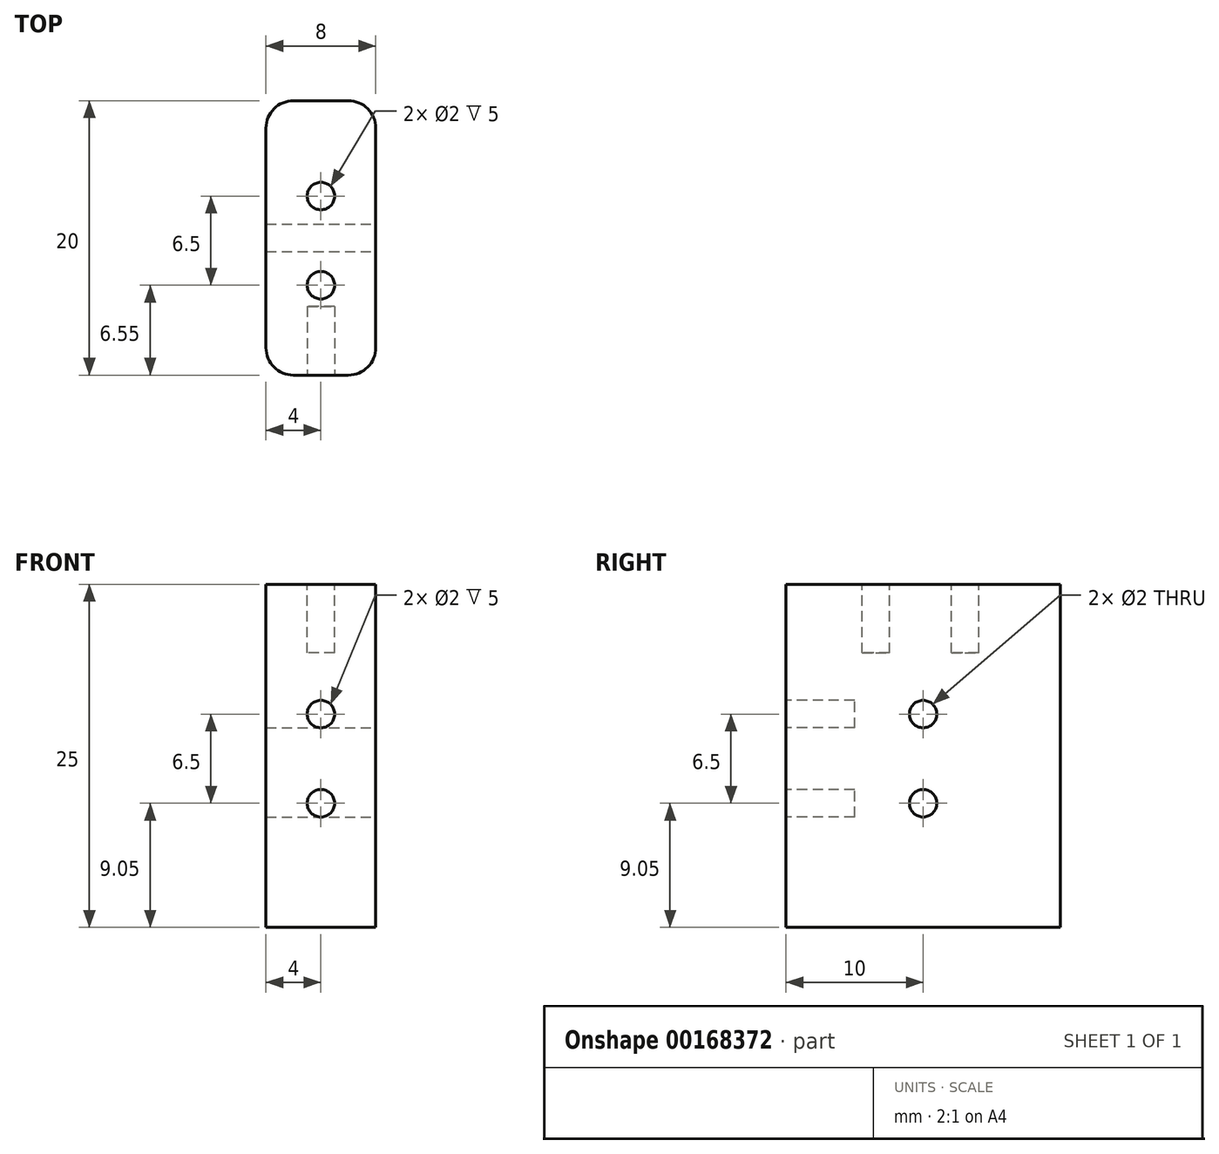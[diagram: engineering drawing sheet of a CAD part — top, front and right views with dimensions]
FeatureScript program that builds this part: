
annotation { "Feature Type Name" : "Feature", "Feature Type Description" : "" }
export const myFeature = defineFeature(function(context is Context, id is Id, definition is map)
    precondition{}
    {
        {
            var Q0;
            Q0=qCreatedBy(makeId("Right.planeOp"),FACE);
            var sketch = newSketch(context, id + "F0", { "sketchPlane" : qUnion([Q0])});
            skLineSegment(sketch, "E0.bottom", {"start": v(10, -12.5) * mm, "end": v(-10, -12.5) * mm});
            skLineSegment(sketch, "E0.top", {"start": v(10, 12.5) * mm, "end": v(-10, 12.5) * mm});
            skLineSegment(sketch, "E0.left", {"start": v(10, -12.5) * mm, "end": v(10, 12.5) * mm});
            skLineSegment(sketch, "E0.right", {"start": v(-10, -12.5) * mm, "end": v(-10, 12.5) * mm});
            skPoint(sketch, "E0.middle", {"position": v(0, 0) * mm});
            skSolve(sketch);
        }
        {
            var Q0;
            Q0 = qSketchRegion(id + "F0", true);
            extrude(context, id + "F1", {"entities" : qUnion([Q0]), "depth" : 8 * mm, "symmetric" : true});
        }
        {
            var Q0;
            Q0=makeQuery(id+"F1.opExtrude","CAP_FACE",FACE,{"disambiguationData":[OSD([sQuery(id+"F0.wireOp",EDGE,"E0.bottom"),sQuery(id+"F0.wireOp",EDGE,"E0.top"),sQuery(id+"F0.wireOp",EDGE,"E0.left"),sQuery(id+"F0.wireOp",EDGE,"E0.right")])],"isStart":false});
            var sketch = newSketch(context, id + "F2", { "sketchPlane" : qUnion([Q0])});
            skCircle(sketch, "E1", {"center": v(0, 3.05) * mm, "radius": 1 * mm});
            skCircle(sketch, "E2", {"center": v(0, -3.45) * mm, "radius": 1 * mm});
            skSolve(sketch);
        }
        {
            var Q0;
            Q0=makeQuery(id+"F1.opExtrude","SWEPT_FACE",FACE,{"disambiguationData":[OSD([sQuery(id+"F0.wireOp",EDGE,"E0.top")])]});
            var sketch = newSketch(context, id + "F3", { "sketchPlane" : qUnion([Q0])});
            skCircle(sketch, "E3", {"center": v(0, 3.05) * mm, "radius": 1 * mm});
            skCircle(sketch, "E4", {"center": v(0, -3.45) * mm, "radius": 1 * mm});
            skSolve(sketch);
        }
        {
            var Q0;
            Q0=makeQuery(id+"F1.opExtrude","SWEPT_FACE",FACE,{"disambiguationData":[OSD([sQuery(id+"F0.wireOp",EDGE,"E0.right")])]});
            var sketch = newSketch(context, id + "F4", { "sketchPlane" : qUnion([Q0])});
            skCircle(sketch, "E5", {"center": v(0, 3.05) * mm, "radius": 1 * mm});
            skCircle(sketch, "E6", {"center": v(0, -3.45) * mm, "radius": 1 * mm});
            skSolve(sketch);
        }
        {
            var Q0;
            Q0=makeQuery(id+"F2.imprint","IMPRINT",FACE,{"disambiguationData":[TD([[makeQuery(id+"F2.imprint","IMPRINT",EDGE,{"derivedFrom":sQuery(id+"F2.wireOp",EDGE,"E1")}),1.0]])]});
            var Q1;
            Q1=makeQuery(id+"F2.imprint","IMPRINT",FACE,{"disambiguationData":[TD([[makeQuery(id+"F2.imprint","IMPRINT",EDGE,{"derivedFrom":sQuery(id+"F2.wireOp",EDGE,"E2")}),1.0]])]});
            extrude(context, id + "F5", {"entities" : qUnion([Q0, Q1]), "operationType" : NewBodyOperationType.REMOVE, "oppositeDirection" : true, "depth" : 25 * mm});
        }
        {
            var Q0;
            Q0=makeQuery(id+"F3.imprint","IMPRINT",FACE,{"disambiguationData":[TD([[makeQuery(id+"F3.imprint","IMPRINT",EDGE,{"derivedFrom":sQuery(id+"F3.wireOp",EDGE,"E4")}),1.0]])]});
            var Q1;
            Q1=makeQuery(id+"F3.imprint","IMPRINT",FACE,{"disambiguationData":[TD([[makeQuery(id+"F3.imprint","IMPRINT",EDGE,{"derivedFrom":sQuery(id+"F3.wireOp",EDGE,"E3")}),1.0]])]});
            extrude(context, id + "F6", {"entities" : qUnion([Q0, Q1]), "operationType" : NewBodyOperationType.REMOVE, "oppositeDirection" : true, "depth" : 5 * mm});
        }
        {
            var Q0;
            Q0=makeQuery(id+"F4.imprint","IMPRINT",FACE,{"disambiguationData":[TD([[makeQuery(id+"F4.imprint","IMPRINT",EDGE,{"derivedFrom":sQuery(id+"F4.wireOp",EDGE,"E5")}),1.0]])]});
            var Q1;
            Q1=makeQuery(id+"F4.imprint","IMPRINT",FACE,{"disambiguationData":[TD([[makeQuery(id+"F4.imprint","IMPRINT",EDGE,{"derivedFrom":sQuery(id+"F4.wireOp",EDGE,"E6")}),1.0]])]});
            extrude(context, id + "F7", {"entities" : qUnion([Q0, Q1]), "operationType" : NewBodyOperationType.REMOVE, "oppositeDirection" : true, "depth" : 5 * mm});
        }
        {
            var Q0;
            Q0=makeQuery(id+"F1.opExtrude","CAP_EDGE",EDGE,{"disambiguationData":[OSD([sQuery(id+"F0.wireOp",EDGE,"E0.right")])],"isStart":false});
            var Q1;
            Q1=makeQuery(id+"F1.opExtrude","CAP_EDGE",EDGE,{"disambiguationData":[OSD([sQuery(id+"F0.wireOp",EDGE,"E0.right")])],"isStart":true});
            var Q2;
            Q2=makeQuery(id+"F1.opExtrude","CAP_EDGE",EDGE,{"disambiguationData":[OSD([sQuery(id+"F0.wireOp",EDGE,"E0.left")])],"isStart":false});
            var Q3;
            Q3=makeQuery(id+"F1.opExtrude","CAP_EDGE",EDGE,{"disambiguationData":[OSD([sQuery(id+"F0.wireOp",EDGE,"E0.left")])],"isStart":true});
            fillet(context, id + "F8", {"entities" : qUnion([Q0, Q1, Q2, Q3]), "radius" : 2 * mm, "tangentPropagation" : true, "allowEdgeOverflow" : false});
        }
    });
